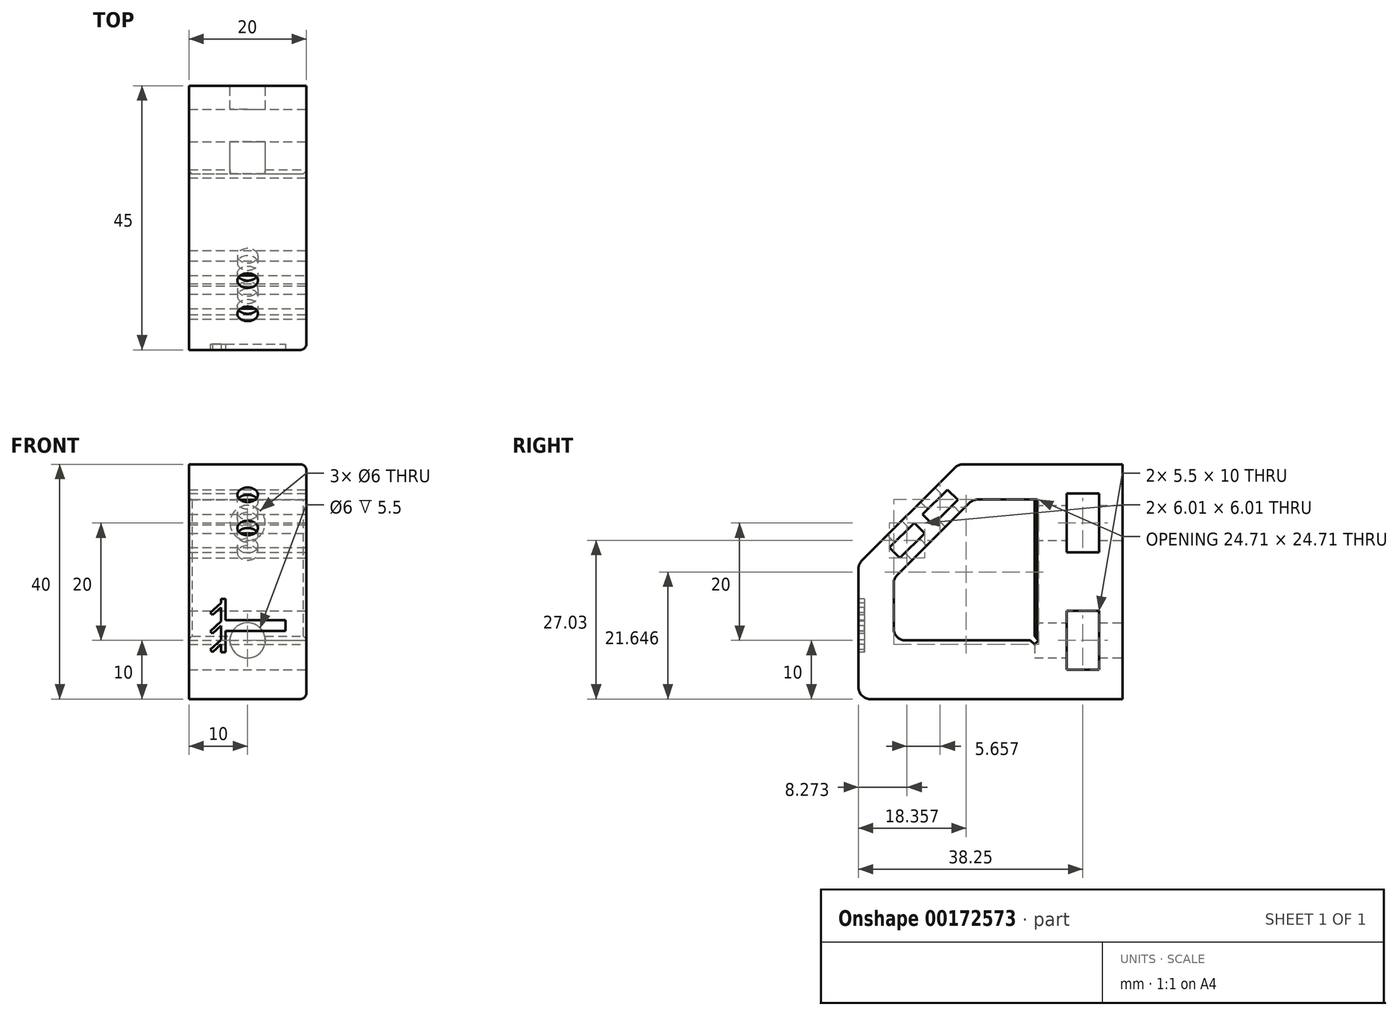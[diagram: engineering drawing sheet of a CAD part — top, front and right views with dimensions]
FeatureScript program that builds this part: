
annotation { "Feature Type Name" : "Feature", "Feature Type Description" : "" }
export const myFeature = defineFeature(function(context is Context, id is Id, definition is map)
    precondition{}
    {
        {
            var Q0;
            Q0=qCreatedBy(makeId("Front.planeOp"),FACE);
            var sketch = newSketch(context, id + "F0", { "sketchPlane" : qUnion([Q0])});
            skLineSegment(sketch, "E0.bottom", {"start": v(0, 0) * mm, "end": v(20, 0) * mm});
            skLineSegment(sketch, "E0.top", {"start": v(0, 40) * mm, "end": v(20, 40) * mm});
            skLineSegment(sketch, "E0.left", {"start": v(0, 0) * mm, "end": v(0, 40) * mm});
            skLineSegment(sketch, "E0.right", {"start": v(20, 0) * mm, "end": v(20, 40) * mm});
            skSolve(sketch);
        }
        {
            var Q0;
            Q0 = qSketchRegion(id + "F0", true);
            extrude(context, id + "F1", {"entities" : qUnion([Q0]), "depth" : 15 * mm});
        }
        {
            var Q0;
            Q0=makeQuery(id+"F1.opExtrude","SWEPT_FACE",FACE,{"disambiguationData":[OSD([sQuery(id+"F0.wireOp",EDGE,"E0.right")])]});
            var sketch = newSketch(context, id + "F2", { "sketchPlane" : qUnion([Q0])});
            skLineSegment(sketch, "E1", {"start": v(-15, 0) * mm, "end": v(-45, 0) * mm});
            skLineSegment(sketch, "E2", {"start": v(-45, 0) * mm, "end": v(-45, 23) * mm});
            skLineSegment(sketch, "E3", {"start": v(-39, 10) * mm, "end": v(-15, 10) * mm});
            skLineSegment(sketch, "E4", {"start": v(-15, 10) * mm, "end": v(-15, 0) * mm});
            skLineSegment(sketch, "E5", {"start": v(-15, 40) * mm, "end": v(-28, 40) * mm});
            skLineSegment(sketch, "E6", {"start": v(-28, 40) * mm, "end": v(-45, 23) * mm});
            skLineSegment(sketch, "E7", {"start": v(-15, 34) * mm, "end": v(-25.51, 34) * mm});
            skLineSegment(sketch, "E8", {"start": v(-25.51, 34) * mm, "end": v(-39, 20.51) * mm});
            skLineSegment(sketch, "E9", {"start": v(-39, 20.51) * mm, "end": v(-39, 10) * mm});
            skSolve(sketch);
        }
        {
            var Q0;
            Q0 = qSketchRegion(id + "F2", true);
            var Q1;
            Q1=makeQuery(id+"F2.imprint","IMPRINT",FACE,{"disambiguationData":[TD([[makeQuery(id+"F2.imprint","IMPRINT",EDGE,{"derivedFrom":sQuery(id+"F2.wireOp",EDGE,"E1")}),-1.0]])]});
            var Q2;
            Q2=makeQuery(id+"F1.opExtrude","SWEPT_FACE",FACE,{"disambiguationData":[OSD([sQuery(id+"F0.wireOp",EDGE,"E0.left")])]});
            extrude(context, id + "F3", {"entities" : qUnion([Q0, Q1]), "operationType" : NewBodyOperationType.ADD, "endBound" : BoundingType.UP_TO_SURFACE, "oppositeDirection" : true, "endBoundEntityFace" : qUnion([Q2]), "depth" : 25 * mm});
        }
        {
            var Q0;
            Q0=makeQuery(id+"F1.opExtrude","CAP_FACE",FACE,{"disambiguationData":[OSD([sQuery(id+"F0.wireOp",EDGE,"E0.bottom"),sQuery(id+"F0.wireOp",EDGE,"E0.top"),sQuery(id+"F0.wireOp",EDGE,"E0.left"),sQuery(id+"F0.wireOp",EDGE,"E0.right")])],"isStart":true});
            var sketch = newSketch(context, id + "F4", { "sketchPlane" : qUnion([Q0])});
            skCircle(sketch, "E10", {"center": v(-10, 30) * mm, "radius": 3 * mm});
            skPoint(sketch, "E10.centerSnap0", {"position": v(-10, 40) * mm});
            skCircle(sketch, "E11", {"center": v(-10, 10) * mm, "radius": 3 * mm});
            skSolve(sketch);
        }
        {
            var Q0;
            Q0 = qSketchRegion(id + "F4", true);
            var Q1;
            Q1=makeQuery(id+"F1.opExtrude","CAP_FACE",FACE,{"disambiguationData":[OSD([sQuery(id+"F0.wireOp",EDGE,"E0.bottom"),sQuery(id+"F0.wireOp",EDGE,"E0.top"),sQuery(id+"F0.wireOp",EDGE,"E0.left"),sQuery(id+"F0.wireOp",EDGE,"E0.right")])],"isStart":false});
            extrude(context, id + "F5", {"entities" : qUnion([Q0]), "operationType" : NewBodyOperationType.REMOVE, "endBound" : BoundingType.UP_TO_SURFACE, "oppositeDirection" : true, "endBoundEntityFace" : qUnion([Q1]), "depth" : 25 * mm});
        }
        {
            var Q0;
            {var subQ0=sQuery(id+"F0.wireOp",EDGE,"E0.right");Q0=makeQuery(id+"F3.boolean.opBoolean","MERGE",FACE,{"derivedFrom":[makeQuery(id+"F1.opExtrude","SWEPT_FACE",FACE,{"disambiguationData":[OSD([subQ0])]}),makeQuery(id+"F3.opExtrude","CAP_FACE",FACE,{"disambiguationData":[OSD([subQ0,sQuery(id+"F2.wireOp",EDGE,"E1"),sQuery(id+"F2.wireOp",EDGE,"E2"),sQuery(id+"F2.wireOp",EDGE,"oFBr16c8-0Q2X-FP0S-YIid-CgedbtGLqJMR"),sQuery(id+"F2.wireOp",EDGE,"evPOPMKi-VTVA-ff8v-8ZP8-QB7idNNDxLJc"),sQuery(id+"F2.wireOp",EDGE,"pkw4sknF-nVUN-RSqT-HF6s-BWwzk2YnTHOt"),sQuery(id+"F2.wireOp",EDGE,"E3"),sQuery(id+"F2.wireOp",EDGE,"E4")])],"isStart":true})]});}
            var sketch = newSketch(context, id + "F6", { "sketchPlane" : qUnion([Q0])});
            skLineSegment(sketch, "E12", {"start": v(-15.7, 10) * mm, "end": v(-15, 9.3) * mm});
            skLineSegment(sketch, "E13", {"start": v(-15, 9.3) * mm, "end": v(-14.29, 10) * mm});
            skLineSegment(sketch, "E14", {"start": v(-14.29, 10) * mm, "end": v(-15, 10.71) * mm});
            skSolve(sketch);
        }
        {
            var Q0;
            Q0 = qSketchRegion(id + "F6", true);
            var Q1;
            {var subQ4=sQuery(id+"F6.wireOp",EDGE,"E12");Q1=makeQuery(id+"F6.imprint","IMPRINT",FACE,{"disambiguationData":[TD([[makeQuery(id+"F6.imprint","IMPRINT",EDGE,{"derivedFrom":subQ4}),1.0]])]});}
            extrude(context, id + "F7", {"entities" : qUnion([Q0, Q1]), "operationType" : NewBodyOperationType.REMOVE, "oppositeDirection" : true, "depth" : 25 * mm});
        }
        {
            var Q0;
            Q0=makeQuery(id+"F3.opExtrude","SWEPT_FACE",FACE,{"disambiguationData":[OSD([sQuery(id+"F2.wireOp",EDGE,"E6")])]});
            var sketch = newSketch(context, id + "F8", { "sketchPlane" : qUnion([Q0])});
            skCircle(sketch, "E15", {"center": v(10, -6.86) * mm, "radius": 1.75 * mm});
            skPoint(sketch, "E15.centerSnap0", {"position": v(10, -15.56) * mm});
            skCircle(sketch, "E16", {"center": v(10, 1.14) * mm, "radius": 1.75 * mm});
            skSolve(sketch);
        }
        {
            var Q0;
            Q0 = qSketchRegion(id + "F8", true);
            extrude(context, id + "F9", {"entities" : qUnion([Q0]), "operationType" : NewBodyOperationType.REMOVE, "endBound" : BoundingType.UP_TO_NEXT, "oppositeDirection" : true, "depth" : 25 * mm});
        }
        {
            var Q0;
            {var subQ0=sQuery(id+"F0.wireOp",EDGE,"E0.right");Q0=makeQuery(id+"F3.boolean.opBoolean","MERGE",FACE,{"derivedFrom":[makeQuery(id+"F1.opExtrude","SWEPT_FACE",FACE,{"disambiguationData":[OSD([subQ0])]}),makeQuery(id+"F3.opExtrude","CAP_FACE",FACE,{"disambiguationData":[OSD([subQ0,sQuery(id+"F2.wireOp",EDGE,"E1"),sQuery(id+"F2.wireOp",EDGE,"E2"),sQuery(id+"F2.wireOp",EDGE,"E3"),sQuery(id+"F2.wireOp",EDGE,"E4"),sQuery(id+"F2.wireOp",EDGE,"E5"),sQuery(id+"F2.wireOp",EDGE,"E6"),sQuery(id+"F2.wireOp",EDGE,"E7"),sQuery(id+"F2.wireOp",EDGE,"E8"),sQuery(id+"F2.wireOp",EDGE,"E9")])],"isStart":true})]});}
            var sketch = newSketch(context, id + "F10", { "sketchPlane" : qUnion([Q0])});
            skLineSegment(sketch, "E17", {"start": v(-39.73, 25.8) * mm, "end": v(-35.49, 30.04) * mm});
            skLineSegment(sketch, "E18", {"start": v(-35.49, 30.04) * mm, "end": v(-33.72, 28.27) * mm});
            skLineSegment(sketch, "E19", {"start": v(-33.72, 28.27) * mm, "end": v(-37.96, 24.03) * mm});
            skLineSegment(sketch, "E20", {"start": v(-37.96, 24.03) * mm, "end": v(-39.73, 25.8) * mm});
            skLineSegment(sketch, "E21", {"start": v(-37.61, 27.91) * mm, "end": v(-35.84, 26.15) * mm, "construction": true});
            skLineSegment(sketch, "E22", {"start": v(-34.08, 31.45) * mm, "end": v(-29.83, 35.7) * mm});
            skLineSegment(sketch, "E23", {"start": v(-29.83, 35.7) * mm, "end": v(-28.06, 33.92) * mm});
            skLineSegment(sketch, "E24", {"start": v(-28.06, 33.92) * mm, "end": v(-32.3, 29.68) * mm});
            skLineSegment(sketch, "E25", {"start": v(-32.3, 29.68) * mm, "end": v(-34.08, 31.45) * mm});
            skLineSegment(sketch, "E26", {"start": v(-31.95, 33.57) * mm, "end": v(-30.19, 31.8) * mm, "construction": true});
            skSolve(sketch);
        }
        {
            var Q0;
            Q0 = qSketchRegion(id + "F10", true);
            extrude(context, id + "F11", {"entities" : qUnion([Q0]), "operationType" : NewBodyOperationType.REMOVE, "oppositeDirection" : true, "depth" : 25 * mm});
        }
        {
            var Q0;
            Q0=makeQuery(id+"F3.opExtrude","SWEPT_EDGE",EDGE,{"disambiguationData":[OSD([sQuery(id+"F2.wireOp",EDGE,"E2"),sQuery(id+"F2.wireOp",EDGE,"E6")])]});
            var Q1;
            Q1=makeQuery(id+"F3.opExtrude","SWEPT_EDGE",EDGE,{"disambiguationData":[OSD([sQuery(id+"F2.wireOp",EDGE,"E1"),sQuery(id+"F2.wireOp",EDGE,"E2")])]});
            var Q2;
            Q2=makeQuery(id+"F3.opExtrude","SWEPT_EDGE",EDGE,{"disambiguationData":[OSD([sQuery(id+"F2.wireOp",EDGE,"E5"),sQuery(id+"F2.wireOp",EDGE,"E6")])]});
            var Q3;
            Q3=makeQuery(id+"F3.opExtrude","SWEPT_EDGE",EDGE,{"disambiguationData":[OSD([sQuery(id+"F2.wireOp",EDGE,"E8"),sQuery(id+"F2.wireOp",EDGE,"E9")])]});
            var Q4;
            Q4=makeQuery(id+"F3.opExtrude","SWEPT_EDGE",EDGE,{"disambiguationData":[OSD([sQuery(id+"F2.wireOp",EDGE,"E7"),sQuery(id+"F2.wireOp",EDGE,"E8")])]});
            var Q5;
            Q5=makeQuery(id+"F3.opExtrude","SWEPT_EDGE",EDGE,{"disambiguationData":[OSD([sQuery(id+"F2.wireOp",EDGE,"E3"),sQuery(id+"F2.wireOp",EDGE,"E9")])]});
            var Q6;
            Q6=makeQuery(id+"F3.opExtrude","SWEPT_EDGE",EDGE,{"disambiguationData":[OSD([sQuery(id+"F0.wireOp",EDGE,"E0.right"),sQuery(id+"F2.wireOp",EDGE,"E7")])]});
            fillet(context, id + "F12", {"entities" : qUnion([Q0, Q1, Q2, Q3, Q4, Q5, Q6]), "radius" : 2 * mm, "tangentPropagation" : true, "allowEdgeOverflow" : false});
        }
        {
            var Q0;
            Q0=makeQuery(id+"F3.opExtrude","CAP_EDGE",EDGE,{"disambiguationData":[OSD([sQuery(id+"F2.wireOp",EDGE,"E6")])],"isStart":true});
            var Q1;
            Q1=makeQuery(id+"F3.opExtrude","TWEAK_EDGE",EDGE,{"derivedFrom":[makeQuery(id+"F1.opExtrude","SWEPT_FACE",FACE,{"disambiguationData":[OSD([sQuery(id+"F0.wireOp",EDGE,"E0.left")])]}),makeQuery(id+"F2.imprint","IMPRINT",EDGE,{"derivedFrom":sQuery(id+"F2.wireOp",EDGE,"E6")})]});
            fillet(context, id + "F13", {"entities" : qUnion([Q0, Q1]), "radius" : 1 * mm, "tangentPropagation" : true, "allowEdgeOverflow" : false});
        }
        {
            var Q0;
            {var subQ0=sQuery(id+"F0.wireOp",EDGE,"E0.right");Q0=makeQuery(id+"F3.boolean.opBoolean","MERGE",FACE,{"derivedFrom":[makeQuery(id+"F1.opExtrude","SWEPT_FACE",FACE,{"disambiguationData":[OSD([subQ0])]}),makeQuery(id+"F3.opExtrude","CAP_FACE",FACE,{"disambiguationData":[OSD([subQ0,sQuery(id+"F2.wireOp",EDGE,"E1"),sQuery(id+"F2.wireOp",EDGE,"E2"),sQuery(id+"F2.wireOp",EDGE,"E3"),sQuery(id+"F2.wireOp",EDGE,"E4"),sQuery(id+"F2.wireOp",EDGE,"E5"),sQuery(id+"F2.wireOp",EDGE,"E6"),sQuery(id+"F2.wireOp",EDGE,"E7"),sQuery(id+"F2.wireOp",EDGE,"E8"),sQuery(id+"F2.wireOp",EDGE,"E9")])],"isStart":true})]});}
            var sketch = newSketch(context, id + "F14", { "sketchPlane" : qUnion([Q0])});
            skLineSegment(sketch, "E27.bottom", {"start": v(-9.5, 35) * mm, "end": v(-4, 35) * mm});
            skLineSegment(sketch, "E27.top", {"start": v(-9.5, 25) * mm, "end": v(-4, 25) * mm});
            skLineSegment(sketch, "E27.left", {"start": v(-9.5, 35) * mm, "end": v(-9.5, 25) * mm});
            skLineSegment(sketch, "E27.right", {"start": v(-4, 35) * mm, "end": v(-4, 25) * mm});
            skLineSegment(sketch, "E28.bottom", {"start": v(-9.5, 15) * mm, "end": v(-4, 15) * mm});
            skLineSegment(sketch, "E28.top", {"start": v(-9.5, 5) * mm, "end": v(-4, 5) * mm});
            skLineSegment(sketch, "E28.left", {"start": v(-9.5, 15) * mm, "end": v(-9.5, 5) * mm});
            skLineSegment(sketch, "E28.right", {"start": v(-4, 15) * mm, "end": v(-4, 5) * mm});
            skSolve(sketch);
        }
        {
            var Q0;
            Q0 = qSketchRegion(id + "F14", true);
            extrude(context, id + "F15", {"entities" : qUnion([Q0]), "operationType" : NewBodyOperationType.REMOVE, "oppositeDirection" : true, "depth" : 25 * mm});
        }
        {
            var Q0;
            Q0=makeQuery(id+"F3.opExtrude","SWEPT_FACE",FACE,{"disambiguationData":[OSD([sQuery(id+"F2.wireOp",EDGE,"E2")])]});
            var sketch = newSketch(context, id + "F16", { "sketchPlane" : qUnion([Q0])});
            skLineSegment(sketch, "E29.bottom", {"start": v(5.46, 17.07) * mm, "end": v(6.26, 17.07) * mm});
            skLineSegment(sketch, "E29.top", {"start": v(5.46, 7.99) * mm, "end": v(6.26, 7.99) * mm});
            skLineSegment(sketch, "E29.left", {"start": v(5.46, 17.07) * mm, "end": v(5.46, 7.99) * mm});
            skLineSegment(sketch, "E29.right", {"start": v(6.26, 17.07) * mm, "end": v(6.26, 7.99) * mm});
            skLineSegment(sketch, "E30.bottom", {"start": v(6.26, 13.45) * mm, "end": v(16.45, 13.45) * mm});
            skLineSegment(sketch, "E30.top", {"start": v(6.26, 11.6) * mm, "end": v(16.45, 11.6) * mm});
            skLineSegment(sketch, "E30.left", {"start": v(6.26, 13.45) * mm, "end": v(6.26, 11.6) * mm});
            skLineSegment(sketch, "E30.right", {"start": v(16.45, 13.45) * mm, "end": v(16.45, 11.6) * mm});
            skLineSegment(sketch, "E31", {"start": v(5.46, 16.4) * mm, "end": v(3.63, 14.72) * mm});
            skLineSegment(sketch, "E32", {"start": v(3.63, 14.72) * mm, "end": v(4.02, 14.3) * mm});
            skLineSegment(sketch, "E33", {"start": v(4.02, 14.3) * mm, "end": v(5.46, 15.62) * mm});
            skLineSegment(sketch, "E34.1.0.0", {"start": v(4.02, 11.15) * mm, "end": v(5.46, 12.47) * mm});
            skLineSegment(sketch, "E34.1.0.1", {"start": v(5.46, 13.24) * mm, "end": v(3.63, 11.57) * mm});
            skLineSegment(sketch, "E34.1.0.2", {"start": v(3.63, 11.57) * mm, "end": v(4.02, 11.15) * mm});
            skLineSegment(sketch, "E34.2.0.0", {"start": v(4.02, 8) * mm, "end": v(5.46, 9.31) * mm});
            skLineSegment(sketch, "E34.2.0.1", {"start": v(5.46, 10.08) * mm, "end": v(3.63, 8.41) * mm});
            skLineSegment(sketch, "E34.2.0.2", {"start": v(3.63, 8.41) * mm, "end": v(4.02, 8) * mm});
            skLineSegment(sketch, "E34.direction1", {"start": v(4.02, 14.3) * mm, "end": v(4.02, 11.15) * mm, "construction": true});
            skSolve(sketch);
        }
        {
            var Q0;
            {var subQ0=sQuery(id+"F16.wireOp",EDGE,"E31");Q0=makeQuery(id+"F16.imprint","IMPRINT",FACE,{"disambiguationData":[TD([[makeQuery(id+"F16.imprint","IMPRINT",EDGE,{"derivedFrom":subQ0}),1.0]])]});}
            var Q1;
            {var subQ8=sQuery(id+"F16.wireOp",EDGE,"E29.bottom");Q1=makeQuery(id+"F16.imprint","IMPRINT",FACE,{"disambiguationData":[TD([[makeQuery(id+"F16.imprint","IMPRINT",EDGE,{"derivedFrom":subQ8}),-1.0]])]});}
            var Q2;
            {var subQ0=sQuery(id+"F16.wireOp",EDGE,"E34.1.0.0");Q2=makeQuery(id+"F16.imprint","IMPRINT",FACE,{"disambiguationData":[TD([[makeQuery(id+"F16.imprint","IMPRINT",EDGE,{"derivedFrom":subQ0}),1.0]])]});}
            var Q3;
            {var subQ0=sQuery(id+"F16.wireOp",EDGE,"E34.2.0.0");Q3=makeQuery(id+"F16.imprint","IMPRINT",FACE,{"disambiguationData":[TD([[makeQuery(id+"F16.imprint","IMPRINT",EDGE,{"derivedFrom":subQ0}),1.0]])]});}
            var Q4;
            Q4=makeQuery(id+"F16.imprint","IMPRINT",FACE,{"disambiguationData":[TD([[makeQuery(id+"F16.imprint","IMPRINT",EDGE,{"derivedFrom":sQuery(id+"F16.wireOp",EDGE,"E30.bottom")}),-1.0]])]});
            extrude(context, id + "F17", {"entities" : qUnion([Q0, Q1, Q2, Q3, Q4]), "operationType" : NewBodyOperationType.REMOVE, "oppositeDirection" : true, "depth" : 1 * mm});
        }
        {
            var Q0;
            Q0=makeQuery(id+"F1.opExtrude","CAP_EDGE",EDGE,{"disambiguationData":[OSD([sQuery(id+"F0.wireOp",EDGE,"E0.right")])],"isStart":false});
            var Q1;
            Q1=makeQuery(id+"F1.opExtrude","CAP_EDGE",EDGE,{"disambiguationData":[OSD([sQuery(id+"F0.wireOp",EDGE,"E0.left")])],"isStart":false});
            chamfer(context, id + "F18", {"entities" : qUnion([Q0, Q1]), "width" : 0.5 * mm, "tangentPropagation" : true});
        }
    });
